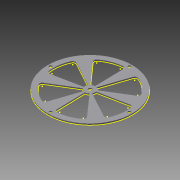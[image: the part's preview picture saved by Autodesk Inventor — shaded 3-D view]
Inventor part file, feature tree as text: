
AUTODESK INVENTOR PART (.ipt)
format: ipt  version: 2013 (Build 170138000, 138)  size: 207,360 bytes
history: native  units: in
note: dims shown in document units (in); Inventor stores cm internally (conversion verified against a paired STEP export)
features: extrude x3, sketch x3, fillet x1
ambient origin geometry x8: Origin, YZ Plane, XZ Plane, XY Plane, X Axis, Y Axis, Z Axis, Center Point
bodies: Solid1 (feature_tree)
feature tree (7):
  extrude  "Extrusion1"  Depth=7.0in
  fillet  "Fillet1"  Radius=0.266in
  extrude  "Extrusion2"  Depth=0.266in
  extrude  "Extrusion3"  Depth=7.5in
  sketch  "Sketch1"  dims[d0=8.0in d1=7.0in d2=0.266in]
  sketch  "Sketch2"  dims[d3=0.266in d4=0.266in]
  sketch  "Sketch3"  dims[d5=0.266in d6=7.5in d7=3.75in d8=3.75in d9=3.75in d10=3.75in d12=1.0in d13=0.375in d14=0.0in d15=0.0in d16=0.1374in d17=2.3622in d19=360.0deg d21=0.125in d22=0.0in d23=0.25in d24=0.315in d25=0.125in d26=0.0in d27=0.0787in d29=0.0394in d30=0.0394in d31=0.25in d32=0.0in]
